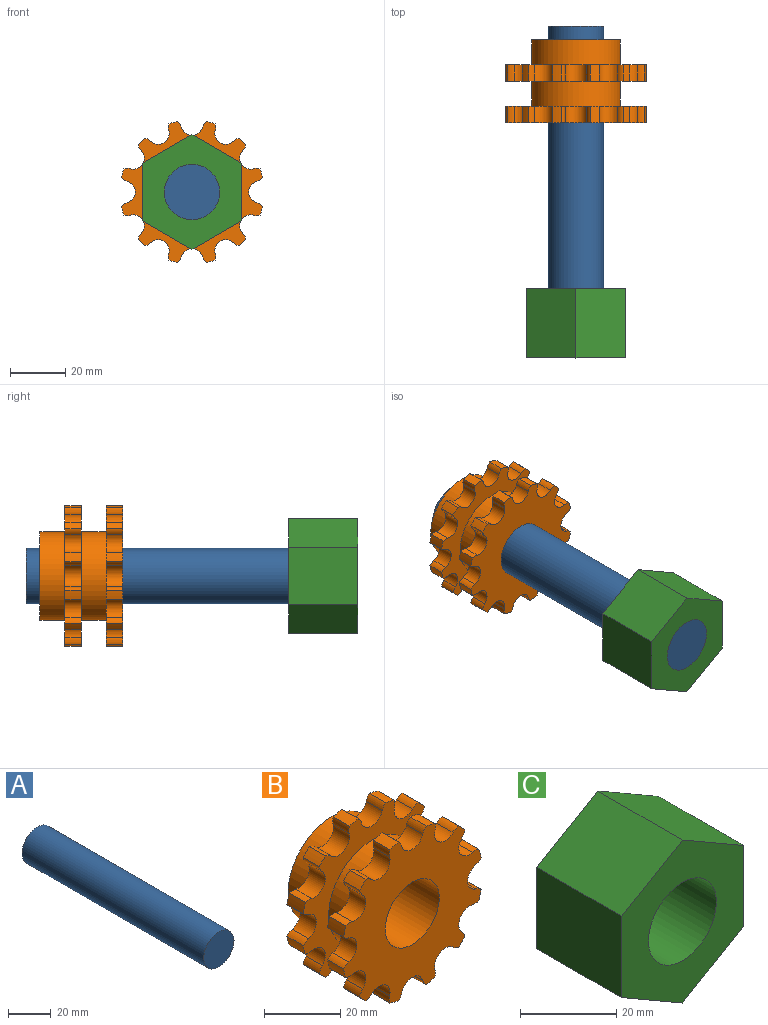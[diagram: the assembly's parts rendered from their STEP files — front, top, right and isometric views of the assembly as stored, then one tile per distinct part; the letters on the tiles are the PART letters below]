
ASSEMBLY  parts=3 mates=2
PART A: 3 faces, bbox 20x120x20 mm
  f0: cylinder r=10mm len=120mm, axis (0,-1,0), area 7539.8mm2, adj f1,f2
  f1: plane 20x20mm, normal (0,1,0), area 314.2mm2, adj f0
  f2: plane 20x20mm, normal (0,-1,0), area 314.2mm2, adj f0
PART B: 104 faces, bbox 51x30x51 mm
  f0: cylinder r=4mm len=6.83mm, axis (0,-1,0), area 62.8mm2, adj f1,f47,f48,f49
  f1: cylinder r=4mm len=6mm, axis (0,-1,0), area 14.3mm2, adj f0,f2,f48,f49
  f2: cylinder r=26mm len=6mm, axis (0,-1,0), area 19.9mm2, adj f1,f3,f48,f49
  f3: cylinder r=4mm len=6mm, axis (0,-1,0), area 14.3mm2, adj f2,f4,f48,f49
  f4: cylinder r=4mm len=7.73mm, axis (0,-1,0), area 62.8mm2, adj f3,f5,f48,f49
  f5: cylinder r=4mm len=6mm, axis (0,-1,0), area 14.3mm2, adj f4,f6,f48,f49
  f6: cylinder r=26mm len=6mm, axis (0,-1,0), area 19.9mm2, adj f5,f7,f48,f49
  f7: cylinder r=4mm len=6mm, axis (0,-1,0), area 14.3mm2, adj f6,f8,f48,f49
  f8: cylinder r=4mm len=6.83mm, axis (0,-1,0), area 62.8mm2, adj f7,f9,f48,f49
  f9: cylinder r=4mm len=6mm, axis (0,-1,0), area 14.3mm2, adj f8,f10,f48,f49
  f10: cylinder r=26mm len=6mm, axis (0,-1,0), area 19.9mm2, adj f9,f11,f48,f49
  f11: cylinder r=4mm len=6mm, axis (0,-1,0), area 14.3mm2, adj f10,f12,f48,f49
  f12: cylinder r=4mm len=6.83mm, axis (0,-1,0), area 62.8mm2, adj f11,f13,f48,f49
  f13: cylinder r=4mm len=6mm, axis (0,-1,0), area 14.3mm2, adj f12,f14,f48,f49
  f14: cylinder r=26mm len=6mm, axis (0,-1,0), area 19.9mm2, adj f13,f15,f48,f49
  f15: cylinder r=4mm len=6mm, axis (0,-1,0), area 14.3mm2, adj f14,f16,f48,f49
  f16: cylinder r=4mm len=7.73mm, axis (0,-1,0), area 62.8mm2, adj f15,f17,f48,f49
  f17: cylinder r=4mm len=6mm, axis (0,-1,0), area 14.3mm2, adj f16,f18,f48,f49
  f18: cylinder r=26mm len=6mm, axis (0,-1,0), area 19.9mm2, adj f17,f19,f48,f49
  f19: cylinder r=4mm len=6mm, axis (0,-1,0), area 14.3mm2, adj f18,f20,f48,f49
  f20: cylinder r=4mm len=6.83mm, axis (0,-1,0), area 62.8mm2, adj f19,f21,f48,f49
  f21: cylinder r=4mm len=6mm, axis (0,-1,0), area 14.3mm2, adj f20,f22,f48,f49
  f22: cylinder r=26mm len=6mm, axis (0,-1,0), area 19.9mm2, adj f21,f23,f48,f49
  f23: cylinder r=4mm len=6mm, axis (0,-1,0), area 14.3mm2, adj f22,f24,f48,f49
  f24: cylinder r=4mm len=6.83mm, axis (0,-1,0), area 62.8mm2, adj f23,f25,f48,f49
  f25: cylinder r=4mm len=6mm, axis (0,-1,0), area 14.3mm2, adj f24,f26,f48,f49
  f26: cylinder r=26mm len=6mm, axis (0,-1,0), area 19.9mm2, adj f25,f27,f48,f49
  f27: cylinder r=4mm len=6mm, axis (0,-1,0), area 14.3mm2, adj f26,f28,f48,f49
  f28: cylinder r=4mm len=7.73mm, axis (0,-1,0), area 62.8mm2, adj f27,f29,f48,f49
  f29: cylinder r=4mm len=6mm, axis (0,-1,0), area 14.3mm2, adj f28,f30,f48,f49
  f30: cylinder r=26mm len=6mm, axis (0,-1,0), area 19.9mm2, adj f29,f31,f48,f49
  f31: cylinder r=4mm len=6mm, axis (0,-1,0), area 14.3mm2, adj f30,f32,f48,f49
  f32: cylinder r=4mm len=6.83mm, axis (0,-1,0), area 62.8mm2, adj f31,f33,f48,f49
  f33: cylinder r=4mm len=6mm, axis (0,-1,0), area 14.3mm2, adj f32,f34,f48,f49
  f34: cylinder r=26mm len=6mm, axis (0,-1,0), area 19.9mm2, adj f33,f35,f48,f49
  f35: cylinder r=4mm len=6mm, axis (0,-1,0), area 14.3mm2, adj f34,f36,f48,f49
  f36: cylinder r=4mm len=6.83mm, axis (0,-1,0), area 62.8mm2, adj f35,f37,f48,f49
  f37: cylinder r=4mm len=6mm, axis (0,-1,0), area 14.3mm2, adj f36,f38,f48,f49
  f38: cylinder r=26mm len=6mm, axis (0,-1,0), area 19.9mm2, adj f37,f39,f48,f49
  f39: cylinder r=4mm len=6mm, axis (0,-1,0), area 14.3mm2, adj f38,f40,f48,f49
  f40: cylinder r=4mm len=7.73mm, axis (0,-1,0), area 62.8mm2, adj f39,f41,f48,f49
  f41: cylinder r=4mm len=6mm, axis (0,-1,0), area 14.3mm2, adj f40,f42,f48,f49
  f42: cylinder r=26mm len=6mm, axis (0,-1,0), area 19.9mm2, adj f41,f43,f48,f49
  f43: cylinder r=4mm len=6mm, axis (0,-1,0), area 14.3mm2, adj f42,f44,f48,f49
  f44: cylinder r=4mm len=6.83mm, axis (0,-1,0), area 62.8mm2, adj f43,f45,f48,f49
  f45: cylinder r=4mm len=6mm, axis (0,-1,0), area 14.3mm2, adj f44,f46,f48,f49
  f46: cylinder r=26mm len=6mm, axis (0,-1,0), area 19.9mm2, adj f45,f47,f48,f49
  f47: cylinder r=4mm len=6mm, axis (0,-1,0), area 14.3mm2, adj f0,f46,f48,f49
  f48: plane 50.98x50.98mm, normal (0,1,0), area 866.5mm2, adj f0,f1,f2,f3,f4,f5,f6,f7
  f49: plane 50.98x50.98mm, normal (0,-1,0), area 866.5mm2, adj f0,f1,f2,f3,f4,f5,f6,f7
  f50: cylinder r=16mm len=32mm, axis (0,-1,0), area 904.8mm2, adj f48,f103
  f51: cylinder r=4mm len=6.83mm, axis (0,-1,0), area 62.8mm2, adj f52,f98,f99,f100
  f52: cylinder r=4mm len=6mm, axis (0,-1,0), area 14.3mm2, adj f51,f53,f99,f100
  f53: cylinder r=26mm len=6mm, axis (0,-1,0), area 19.9mm2, adj f52,f54,f99,f100
  f54: cylinder r=4mm len=6mm, axis (0,-1,0), area 14.3mm2, adj f53,f55,f99,f100
  f55: cylinder r=4mm len=7.73mm, axis (0,-1,0), area 62.8mm2, adj f54,f56,f99,f100
  f56: cylinder r=4mm len=6mm, axis (0,-1,0), area 14.3mm2, adj f55,f57,f99,f100
  f57: cylinder r=26mm len=6mm, axis (0,-1,0), area 19.9mm2, adj f56,f58,f99,f100
  f58: cylinder r=4mm len=6mm, axis (0,-1,0), area 14.3mm2, adj f57,f59,f99,f100
  f59: cylinder r=4mm len=6.83mm, axis (0,-1,0), area 62.8mm2, adj f58,f60,f99,f100
  f60: cylinder r=4mm len=6mm, axis (0,-1,0), area 14.3mm2, adj f59,f61,f99,f100
  f61: cylinder r=26mm len=6mm, axis (0,-1,0), area 19.9mm2, adj f60,f62,f99,f100
  f62: cylinder r=4mm len=6mm, axis (0,-1,0), area 14.3mm2, adj f61,f63,f99,f100
  f63: cylinder r=4mm len=6.83mm, axis (0,-1,0), area 62.8mm2, adj f62,f64,f99,f100
  f64: cylinder r=4mm len=6mm, axis (0,-1,0), area 14.3mm2, adj f63,f65,f99,f100
  f65: cylinder r=26mm len=6mm, axis (0,-1,0), area 19.9mm2, adj f64,f66,f99,f100
  f66: cylinder r=4mm len=6mm, axis (0,-1,0), area 14.3mm2, adj f65,f67,f99,f100
  f67: cylinder r=4mm len=7.73mm, axis (0,-1,0), area 62.8mm2, adj f66,f68,f99,f100
  f68: cylinder r=4mm len=6mm, axis (0,-1,0), area 14.3mm2, adj f67,f69,f99,f100
  f69: cylinder r=26mm len=6mm, axis (0,-1,0), area 19.9mm2, adj f68,f70,f99,f100
  f70: cylinder r=4mm len=6mm, axis (0,-1,0), area 14.3mm2, adj f69,f71,f99,f100
  f71: cylinder r=4mm len=6.83mm, axis (0,-1,0), area 62.8mm2, adj f70,f72,f99,f100
  f72: cylinder r=4mm len=6mm, axis (0,-1,0), area 14.3mm2, adj f71,f73,f99,f100
  f73: cylinder r=26mm len=6mm, axis (0,-1,0), area 19.9mm2, adj f72,f74,f99,f100
  f74: cylinder r=4mm len=6mm, axis (0,-1,0), area 14.3mm2, adj f73,f75,f99,f100
  f75: cylinder r=4mm len=6.83mm, axis (0,-1,0), area 62.8mm2, adj f74,f76,f99,f100
  f76: cylinder r=4mm len=6mm, axis (0,-1,0), area 14.3mm2, adj f75,f77,f99,f100
  f77: cylinder r=26mm len=6mm, axis (0,-1,0), area 19.9mm2, adj f76,f78,f99,f100
  f78: cylinder r=4mm len=6mm, axis (0,-1,0), area 14.3mm2, adj f77,f79,f99,f100
  f79: cylinder r=4mm len=7.73mm, axis (0,-1,0), area 62.8mm2, adj f78,f80,f99,f100
  f80: cylinder r=4mm len=6mm, axis (0,-1,0), area 14.3mm2, adj f79,f81,f99,f100
  f81: cylinder r=26mm len=6mm, axis (0,-1,0), area 19.9mm2, adj f80,f82,f99,f100
  f82: cylinder r=4mm len=6mm, axis (0,-1,0), area 14.3mm2, adj f81,f83,f99,f100
  f83: cylinder r=4mm len=6.83mm, axis (0,-1,0), area 62.8mm2, adj f82,f84,f99,f100
  f84: cylinder r=4mm len=6mm, axis (0,-1,0), area 14.3mm2, adj f83,f85,f99,f100
  f85: cylinder r=26mm len=6mm, axis (0,-1,0), area 19.9mm2, adj f84,f86,f99,f100
  f86: cylinder r=4mm len=6mm, axis (0,-1,0), area 14.3mm2, adj f85,f87,f99,f100
  f87: cylinder r=4mm len=6.83mm, axis (0,-1,0), area 62.8mm2, adj f86,f88,f99,f100
  f88: cylinder r=4mm len=6mm, axis (0,-1,0), area 14.3mm2, adj f87,f89,f99,f100
  f89: cylinder r=26mm len=6mm, axis (0,-1,0), area 19.9mm2, adj f88,f90,f99,f100
  f90: cylinder r=4mm len=6mm, axis (0,-1,0), area 14.3mm2, adj f89,f91,f99,f100
  f91: cylinder r=4mm len=7.73mm, axis (0,-1,0), area 62.8mm2, adj f90,f92,f99,f100
  f92: cylinder r=4mm len=6mm, axis (0,-1,0), area 14.3mm2, adj f91,f93,f99,f100
  f93: cylinder r=26mm len=6mm, axis (0,-1,0), area 19.9mm2, adj f92,f94,f99,f100
  f94: cylinder r=4mm len=6mm, axis (0,-1,0), area 14.3mm2, adj f93,f95,f99,f100
  f95: cylinder r=4mm len=6.83mm, axis (0,-1,0), area 62.8mm2, adj f94,f96,f99,f100
  f96: cylinder r=4mm len=6mm, axis (0,-1,0), area 14.3mm2, adj f95,f97,f99,f100
  f97: cylinder r=26mm len=6mm, axis (0,-1,0), area 19.9mm2, adj f96,f98,f99,f100
  f98: cylinder r=4mm len=6mm, axis (0,-1,0), area 14.3mm2, adj f51,f97,f99,f100
  f99: plane 50.98x50.98mm, normal (0,1,0), area 866.5mm2, adj f51,f52,f53,f54,f55,f56,f57,f58
  f100: plane 50.98x50.98mm, normal (0,-1,0), area 1356.6mm2, adj f51,f52,f53,f54,f55,f56,f57,f58
  f101: cylinder r=16mm len=32mm, axis (0,-1,0), area 904.8mm2, adj f49,f99
  f102: cylinder r=10mm len=30mm, axis (0,-1,0), area 1885mm2, adj f100,f103
  f103: plane 32x32mm, normal (0,1,0), area 490.1mm2, adj f50,f102
PART C: 9 faces, bbox 36x25x41.6 mm
  f0: plane 25x20.78mm, normal (-1,0,0), area 519.6mm2, adj f1,f6,f7,f8
  f1: plane 25x18mm, normal (-0.5,0,-0.87), area 519.6mm2, adj f0,f2,f7,f8
  f2: plane 25x18mm, normal (0.5,0,-0.87), area 519.6mm2, adj f1,f3,f7,f8
  f3: plane 25x20.78mm, normal (1,0,0), area 519.6mm2, adj f2,f4,f7,f8
  f4: plane 25x18mm, normal (0.5,0,0.87), area 519.6mm2, adj f3,f6,f7,f8
  f5: cylinder r=10mm len=25mm, axis (0,-1,0), area 1570.8mm2, adj f7,f8
  f6: plane 25x18mm, normal (-0.5,0,0.87), area 519.6mm2, adj f0,f4,f7,f8
  f7: plane 41.57x36mm, normal (0,1,0), area 808.2mm2, adj f0,f1,f2,f3,f4,f5,f6
  f8: plane 41.57x36mm, normal (0,-1,0), area 808.2mm2, adj f0,f1,f2,f3,f4,f5,f6
PLACE A t=(8.84,-118.71,-5.24)mm
PLACE B t=(8.84,-33.71,-5.24)mm
PLACE C t=(8.84,-118.71,-5.24)mm
MATE fastened A.f0 <-> B.f102  axis (0,1,0) through (8.84,1.29,-5.24)mm
MATE fastened C.f5 <-> A.f0  axis (0,-1,0) through (8.84,-118.71,-5.24)mm
